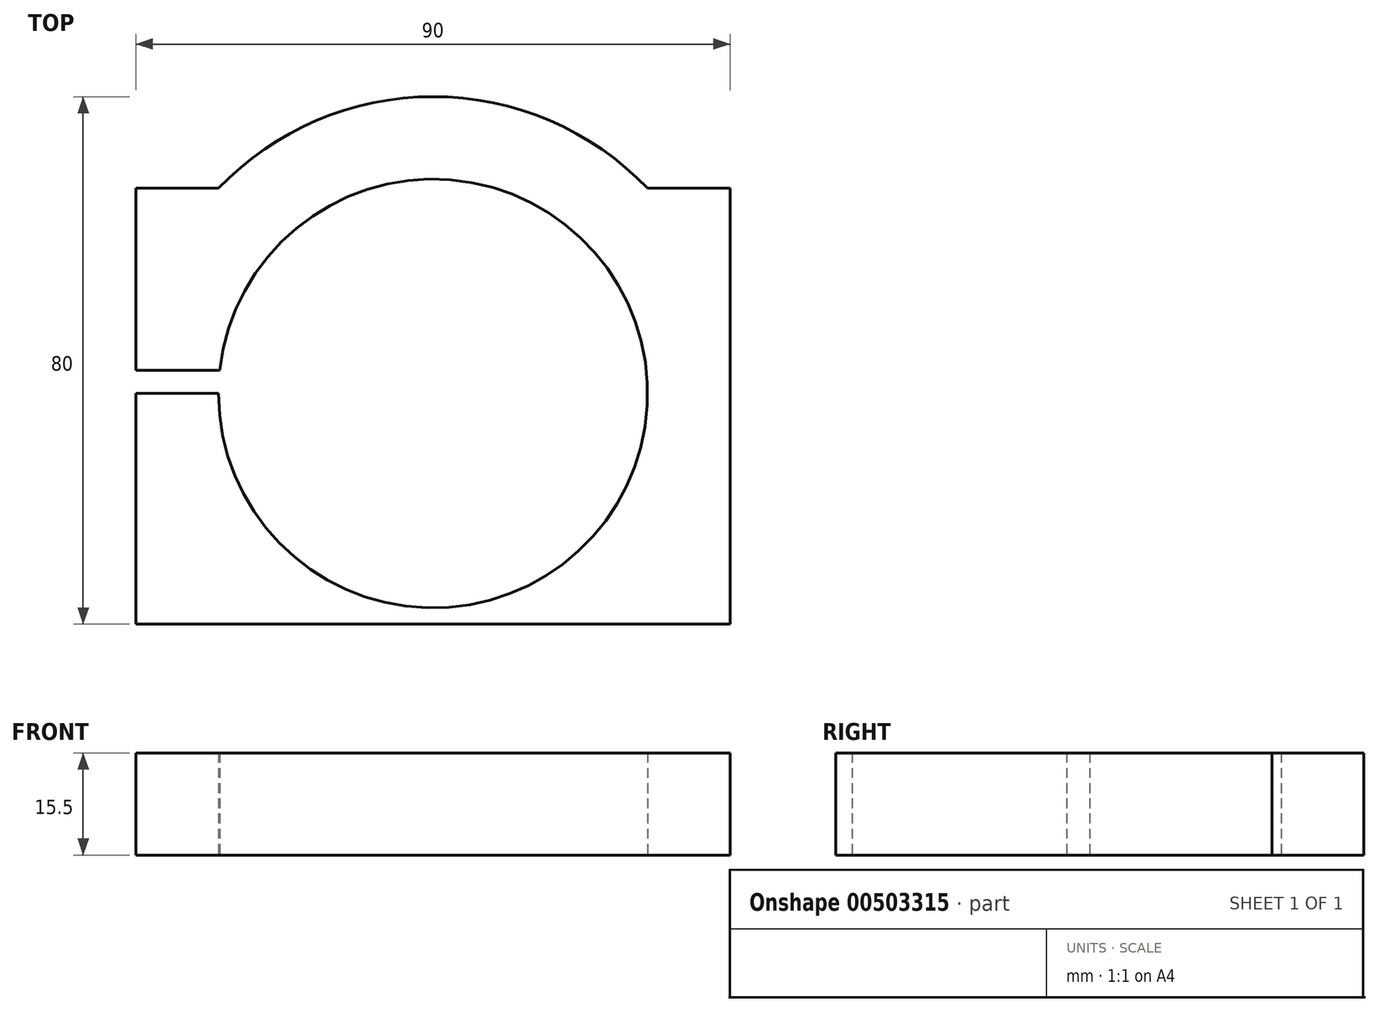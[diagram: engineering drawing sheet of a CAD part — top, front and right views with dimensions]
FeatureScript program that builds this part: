
annotation { "Feature Type Name" : "Feature", "Feature Type Description" : "" }
export const myFeature = defineFeature(function(context is Context, id is Id, definition is map)
    precondition{}
    {
        {
            var Q0;
            Q0=qCreatedBy(makeId("Top.planeOp"),FACE);
            var sketch = newSketch(context, id + "F0", { "sketchPlane" : qUnion([Q0])});
            skLineSegment(sketch, "E0.bottom", {"start": v(0, 0) * mm, "end": v(90, 0) * mm});
            skLineSegment(sketch, "E0.left", {"start": v(0, 0) * mm, "end": v(0, 35) * mm});
            skLineSegment(sketch, "E0.right", {"start": v(90, 0) * mm, "end": v(90, 35) * mm});
            skArc(sketch, "E1", {"start": v(77.31, 38.5) * mm, "mid": v(45, 67.5) * mm, "end": v(12.69, 38.5) * mm});
            skArc(sketch, "E2", {"start": v(77.5, 66.13) * mm, "mid": v(45, 80) * mm, "end": v(12.5, 66.13) * mm});
            skLineSegment(sketch, "E3", {"start": v(90, 38.5) * mm, "end": v(90, 66.13) * mm});
            skLineSegment(sketch, "E4", {"start": v(90, 66.13) * mm, "end": v(77.5, 66.13) * mm});
            skLineSegment(sketch, "E5", {"start": v(0, 38.5) * mm, "end": v(0, 66.13) * mm});
            skLineSegment(sketch, "E6.trimOffspring", {"start": v(12.5, 66.13) * mm, "end": v(0, 66.13) * mm});
            skLineSegment(sketch, "E7", {"start": v(0, 35) * mm, "end": v(12.5, 35) * mm});
            skLineSegment(sketch, "E8", {"start": v(0, 38.5) * mm, "end": v(12.69, 38.5) * mm});
            skArc(sketch, "E9.trimOffspring", {"start": v(12.5, 35) * mm, "mid": v(45, 2.5) * mm, "end": v(77.5, 35) * mm});
            skArc(sketch, "E10", {"start": v(12.5, 35) * mm, "mid": v(77.45, 33.25) * mm, "end": v(12.69, 38.5) * mm});
            skLineSegment(sketch, "E11", {"start": v(90, 38.5) * mm, "end": v(90, 35) * mm});
            skSolve(sketch);
        }
        {
            var Q0;
            Q0 = qSketchRegion(id + "F0", true);
            extrude(context, id + "F1", {"entities" : qUnion([Q0]), "depth" : 15.5 * mm});
        }
    });
